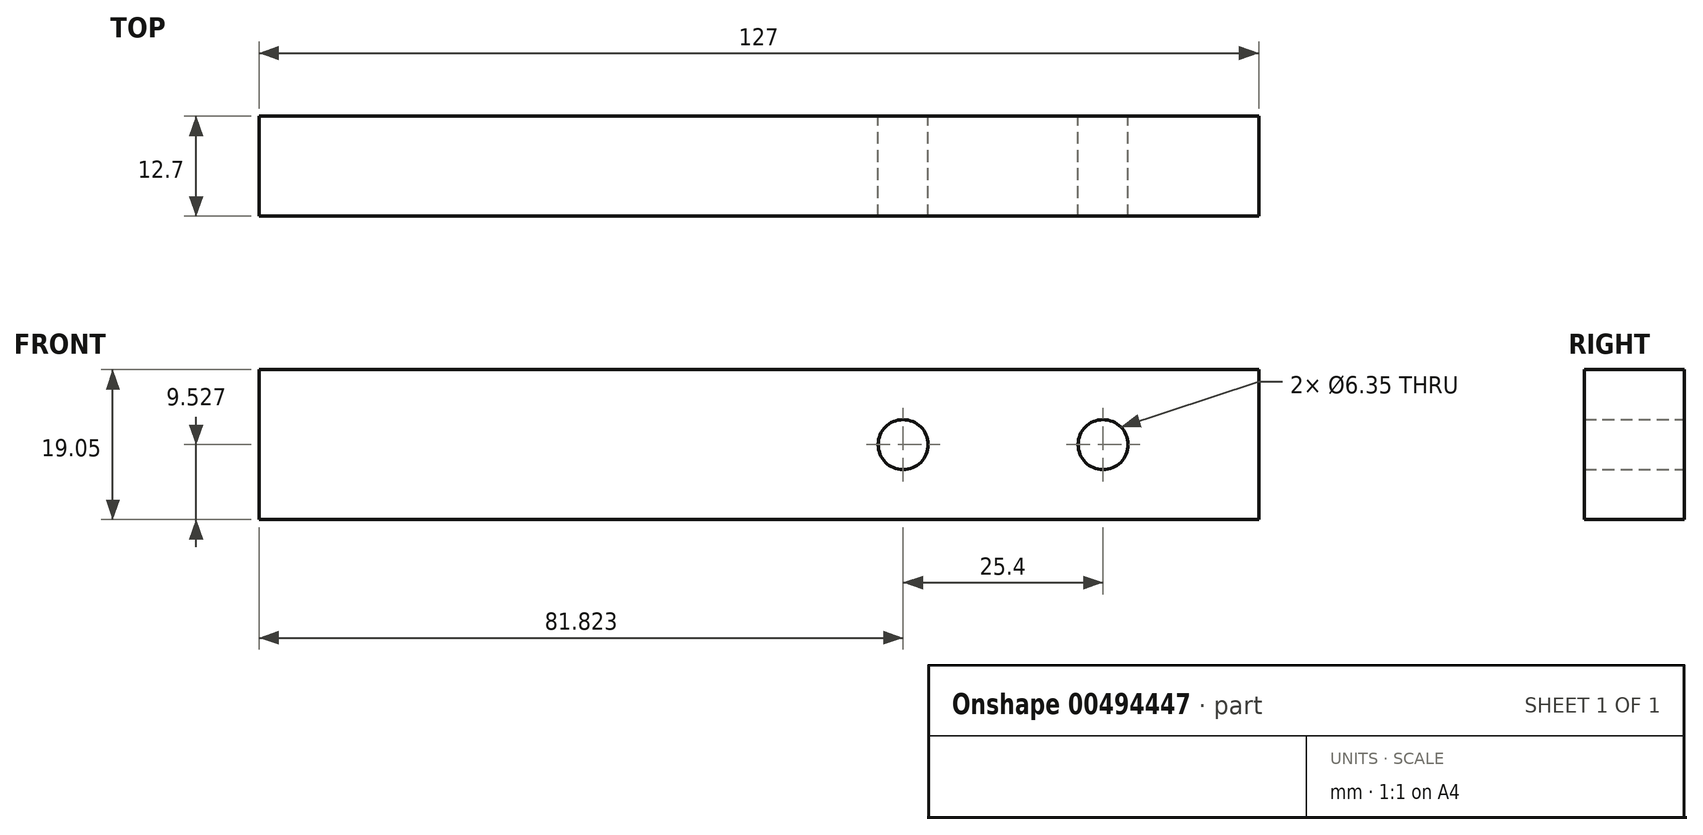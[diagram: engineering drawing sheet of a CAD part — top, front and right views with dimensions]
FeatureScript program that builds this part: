
annotation { "Feature Type Name" : "Feature", "Feature Type Description" : "" }
export const myFeature = defineFeature(function(context is Context, id is Id, definition is map)
    precondition{}
    {
        {
            var Q0;
            Q0=qCreatedBy(makeId("Front.planeOp"),FACE);
            var sketch = newSketch(context, id + "F0", { "sketchPlane" : qUnion([Q0])});
            skLineSegment(sketch, "E0.bottom", {"start": v(-142.77, 27.84) * mm, "end": v(-15.77, 27.84) * mm});
            skLineSegment(sketch, "E0.top", {"start": v(-142.77, 8.8) * mm, "end": v(-15.77, 8.8) * mm});
            skLineSegment(sketch, "E0.left", {"start": v(-142.77, 27.84) * mm, "end": v(-142.77, 8.8) * mm});
            skLineSegment(sketch, "E0.right", {"start": v(-15.77, 27.84) * mm, "end": v(-15.77, 8.8) * mm});
            skCircle(sketch, "E1", {"center": v(-35.55, 18.32) * mm, "radius": 3.18 * mm});
            skLineSegment(sketch, "E2", {"start": v(-60.75, 36.03) * mm, "end": v(-16.3, 36.03) * mm});
            skCircle(sketch, "E3", {"center": v(-60.95, 18.32) * mm, "radius": 3.18 * mm});
            skSolve(sketch);
        }
        {
            var Q0;
            Q0 = qSketchRegion(id + "F0", true);
            extrude(context, id + "F1", {"entities" : qUnion([Q0]), "depth" : 12.7 * mm});
        }
    });
